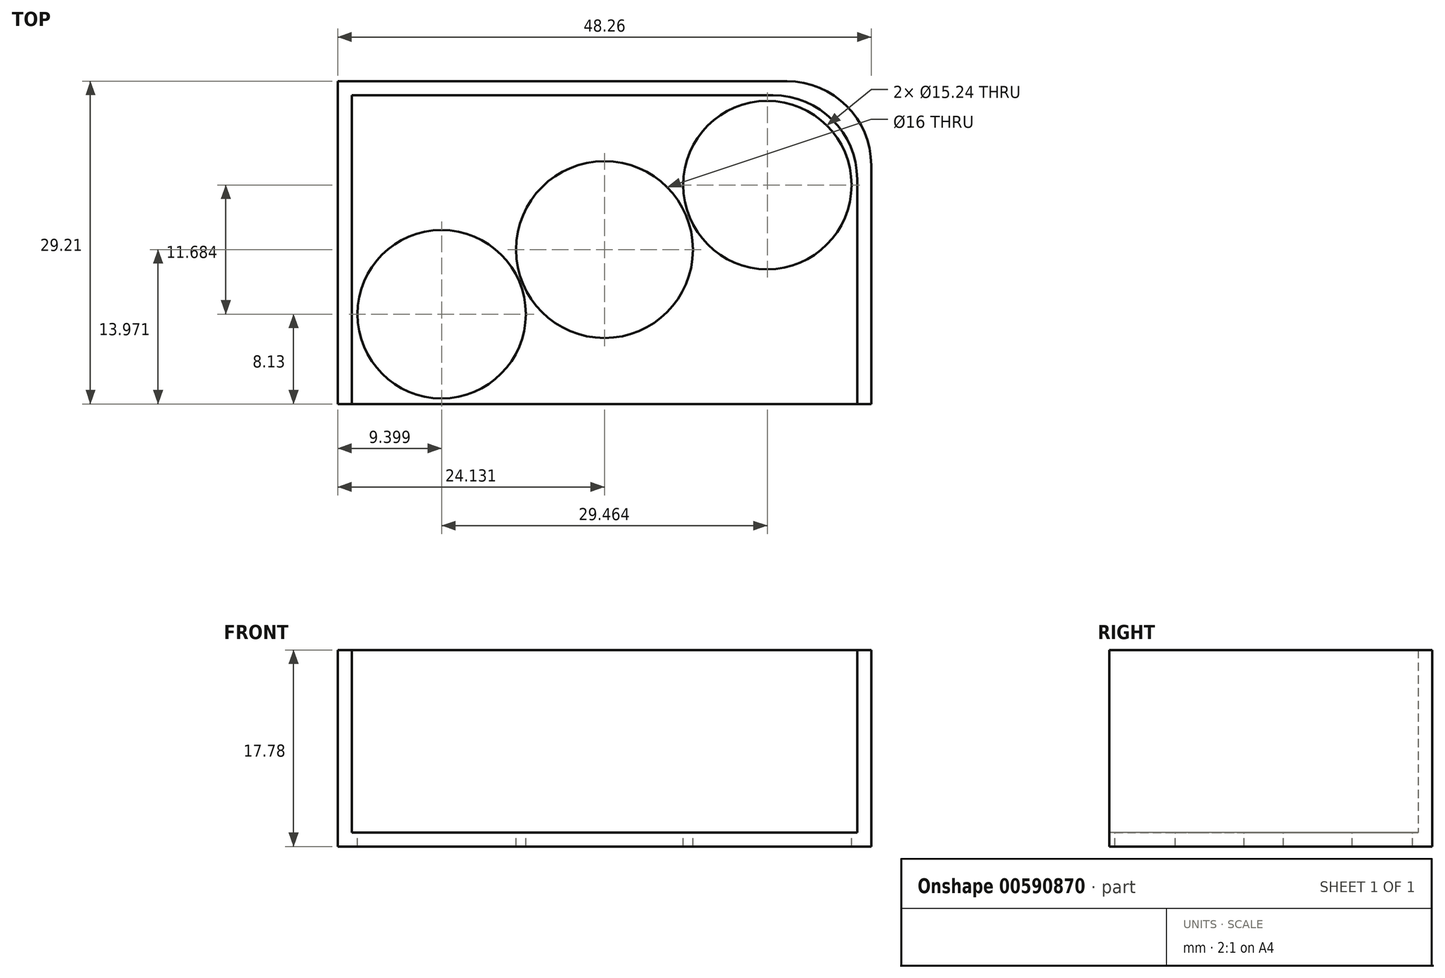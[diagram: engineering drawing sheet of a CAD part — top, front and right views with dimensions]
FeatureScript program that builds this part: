
annotation { "Feature Type Name" : "Feature", "Feature Type Description" : "" }
export const myFeature = defineFeature(function(context is Context, id is Id, definition is map)
    precondition{}
    {
        {
            var Q0;
            Q0=qCreatedBy(makeId("Top.planeOp"),FACE);
            var sketch = newSketch(context, id + "F0", { "sketchPlane" : qUnion([Q0])});
            skLineSegment(sketch, "E0.bottom", {"start": v(-64.95, 15.68) * mm, "end": v(-16.69, 15.68) * mm});
            skLineSegment(sketch, "E0.top", {"start": v(-64.95, -14.8) * mm, "end": v(-16.69, -14.8) * mm});
            skLineSegment(sketch, "E0.left", {"start": v(-64.95, 15.68) * mm, "end": v(-64.95, -14.8) * mm});
            skLineSegment(sketch, "E0.right", {"start": v(-16.69, 15.68) * mm, "end": v(-16.69, -14.8) * mm});
            skLineSegment(sketch, "E1.bottom", {"start": v(-63.68, 14.41) * mm, "end": v(-17.96, 14.41) * mm});
            skLineSegment(sketch, "E1.top", {"start": v(-63.68, -13.53) * mm, "end": v(-17.96, -13.53) * mm});
            skLineSegment(sketch, "E1.left", {"start": v(-63.68, 14.41) * mm, "end": v(-63.68, -13.53) * mm});
            skLineSegment(sketch, "E1.right", {"start": v(-17.96, 14.41) * mm, "end": v(-17.96, -13.53) * mm});
            skSolve(sketch);
        }
        {
            var Q0;
            Q0=makeQuery(id+"F0.imprint","IMPRINT",FACE,{"disambiguationData":[TD([[makeQuery(id+"F0.imprint","IMPRINT",EDGE,{"derivedFrom":sQuery(id+"F0.wireOp",EDGE,"E0.bottom")}),-1.0]])]});
            extrude(context, id + "F1", {"entities" : qUnion([Q0]), "depth" : 17.78 * mm, "offsetDistance" : 25.4 * mm});
        }
        {
            var Q0;
            Q0=makeQuery(id+"F0.imprint","IMPRINT",FACE,{"disambiguationData":[TD([[makeQuery(id+"F0.imprint","IMPRINT",EDGE,{"derivedFrom":sQuery(id+"F0.wireOp",EDGE,"E1.bottom")}),-1.0]])]});
            extrude(context, id + "F2", {"entities" : qUnion([Q0]), "operationType" : NewBodyOperationType.ADD, "depth" : 1.27 * mm, "offsetDistance" : 25.4 * mm});
        }
        {
            var Q0;
            Q0=makeQuery(id+"F1.opExtrude","SWEPT_EDGE",EDGE,{"disambiguationData":[OSD([sQuery(id+"F0.wireOp",EDGE,"E0.bottom"),sQuery(id+"F0.wireOp",EDGE,"E0.right")])]});
            var Q1;
            Q1=makeQuery(id+"F1.opExtrude","SWEPT_EDGE",EDGE,{"disambiguationData":[OSD([sQuery(id+"F0.wireOp",EDGE,"E1.bottom"),sQuery(id+"F0.wireOp",EDGE,"E1.right")])]});
            fillet(context, id + "F3", {"entities" : qUnion([Q0, Q1]), "radius" : 7.62 * mm, "tangentPropagation" : true, "allowEdgeOverflow" : false});
        }
        {
            var Q0;
            Q0=makeQuery(id+"F2.opExtrude","CAP_FACE",FACE,{"disambiguationData":[OSD([sQuery(id+"F0.wireOp",EDGE,"E1.bottom"),sQuery(id+"F0.wireOp",EDGE,"E1.top"),sQuery(id+"F0.wireOp",EDGE,"E1.left"),sQuery(id+"F0.wireOp",EDGE,"E1.right")])],"isStart":false});
            var sketch = newSketch(context, id + "F4", { "sketchPlane" : qUnion([Q0])});
            skCircle(sketch, "E2", {"center": v(-40.82, 0.44) * mm, "radius": 8 * mm});
            skCircle(sketch, "E3", {"center": v(-26.09, 6.28) * mm, "radius": 7.62 * mm});
            skCircle(sketch, "E4", {"center": v(-55.55, -5.4) * mm, "radius": 7.62 * mm});
            skSolve(sketch);
        }
        {
            var Q0;
            Q0=makeQuery(id+"F1.opExtrude","SWEPT_FACE",FACE,{"disambiguationData":[OSD([sQuery(id+"F0.wireOp",EDGE,"E0.top")])]});
            var sketch = newSketch(context, id + "F5", { "sketchPlane" : qUnion([Q0])});
            skLineSegment(sketch, "E5.bottom", {"start": v(-64.95, 17.78) * mm, "end": v(-16.69, 17.78) * mm});
            skLineSegment(sketch, "E5.top", {"start": v(-64.95, 0) * mm, "end": v(-16.69, 0) * mm});
            skLineSegment(sketch, "E5.left", {"start": v(-64.95, 17.78) * mm, "end": v(-64.95, 0) * mm});
            skLineSegment(sketch, "E5.right", {"start": v(-16.69, 17.78) * mm, "end": v(-16.69, 0) * mm});
            skSolve(sketch);
        }
        {
            var Q0;
            Q0 = qSketchRegion(id + "F5", true);
            extrude(context, id + "F6", {"entities" : qUnion([Q0]), "operationType" : NewBodyOperationType.REMOVE, "oppositeDirection" : true, "depth" : 1.27 * mm, "offsetDistance" : 25.4 * mm});
        }
        {
            var Q0;
            Q0 = qSketchRegion(id + "F4", true);
            extrude(context, id + "F7", {"entities" : qUnion([Q0]), "operationType" : NewBodyOperationType.REMOVE, "oppositeDirection" : true, "depth" : 12.17 * mm, "offsetDistance" : 25.4 * mm});
        }
    });
